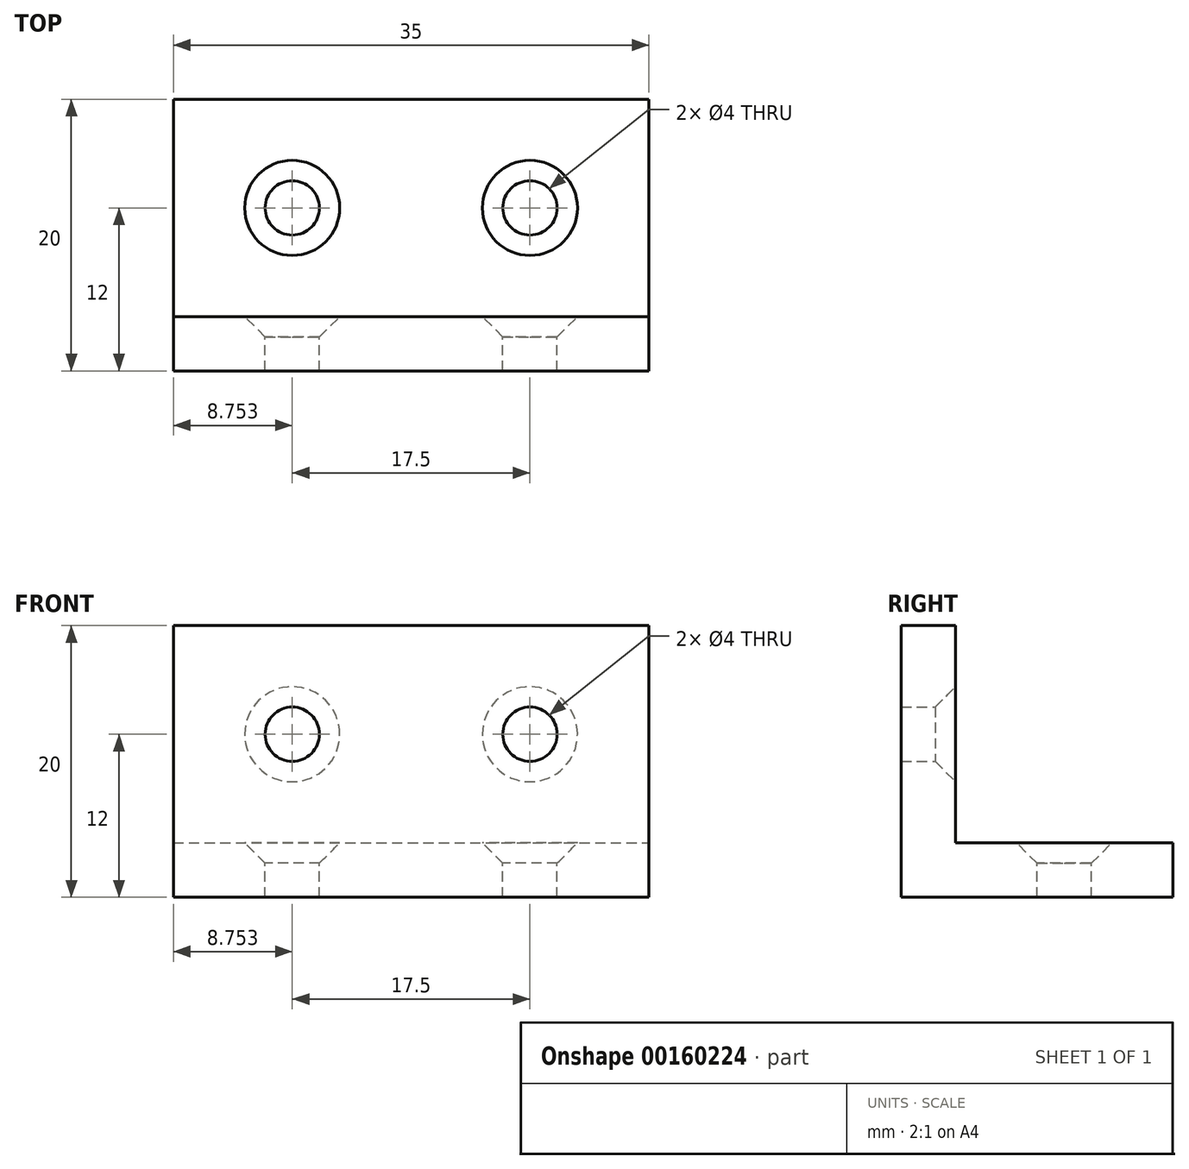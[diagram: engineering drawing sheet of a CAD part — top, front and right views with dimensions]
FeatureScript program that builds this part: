
annotation { "Feature Type Name" : "Feature", "Feature Type Description" : "" }
export const myFeature = defineFeature(function(context is Context, id is Id, definition is map)
    precondition{}
    {
        {
            var Q0;
            Q0=qCreatedBy(makeId("Top.planeOp"),FACE);
            var sketch = newSketch(context, id + "F0", { "sketchPlane" : qUnion([Q0])});
            skLineSegment(sketch, "E0.bottom", {"start": v(-15.22, 0) * mm, "end": v(19.78, 0) * mm});
            skLineSegment(sketch, "E0.top", {"start": v(-15.22, 20) * mm, "end": v(19.78, 20) * mm});
            skLineSegment(sketch, "E0.left", {"start": v(-15.22, 0) * mm, "end": v(-15.22, 20) * mm});
            skLineSegment(sketch, "E0.right", {"start": v(19.78, 0) * mm, "end": v(19.78, 20) * mm});
            skSolve(sketch);
        }
        {
            var Q0;
            Q0=makeQuery(id+"F0.imprint","IMPRINT",FACE,{"disambiguationData":[TD([[makeQuery(id+"F0.imprint","IMPRINT",EDGE,{"derivedFrom":sQuery(id+"F0.wireOp",EDGE,"E0.bottom")}),1.0]])]});
            extrude(context, id + "F1", {"entities" : qUnion([Q0]), "depth" : 4 * mm});
        }
        {
            var Q0;
            Q0=makeQuery(id+"F1.opExtrude","CAP_FACE",FACE,{"disambiguationData":[OSD([sQuery(id+"F0.wireOp",EDGE,"E0.bottom"),sQuery(id+"F0.wireOp",EDGE,"E0.top"),sQuery(id+"F0.wireOp",EDGE,"E0.left"),sQuery(id+"F0.wireOp",EDGE,"E0.right")])],"isStart":false});
            var sketch = newSketch(context, id + "F2", { "sketchPlane" : qUnion([Q0])});
            skLineSegment(sketch, "E1.bottom", {"start": v(-15.22, 0) * mm, "end": v(19.78, 0) * mm});
            skLineSegment(sketch, "E1.top", {"start": v(-15.22, 4) * mm, "end": v(19.78, 4) * mm});
            skLineSegment(sketch, "E1.left", {"start": v(-15.22, 0) * mm, "end": v(-15.22, 4) * mm});
            skLineSegment(sketch, "E1.right", {"start": v(19.78, 0) * mm, "end": v(19.78, 4) * mm});
            skSolve(sketch);
        }
        {
            var Q0;
            Q0=makeQuery(id+"F2.imprint","IMPRINT",FACE,{"disambiguationData":[TD([[makeQuery(id+"F2.imprint","IMPRINT",EDGE,{"derivedFrom":sQuery(id+"F2.wireOp",EDGE,"E1.bottom")}),1.0]])]});
            extrude(context, id + "F3", {"entities" : qUnion([Q0]), "operationType" : NewBodyOperationType.ADD, "depth" : 16 * mm});
        }
        {
            var Q0;
            Q0=makeQuery(id+"F3.opExtrude","SWEPT_FACE",FACE,{"disambiguationData":[OSD([sQuery(id+"F2.wireOp",EDGE,"E1.top")])]});
            var sketch = newSketch(context, id + "F4", { "sketchPlane" : qUnion([Q0])});
            skPoint(sketch, "E2", {"position": v(-11.03, 12) * mm});
            skPoint(sketch, "E3", {"position": v(6.47, 12) * mm});
            skSolve(sketch);
        }
        {
            var Q0;
            Q0=makeQuery(id+"F1.opExtrude","CAP_FACE",FACE,{"disambiguationData":[OSD([sQuery(id+"F0.wireOp",EDGE,"E0.bottom"),sQuery(id+"F0.wireOp",EDGE,"E0.top"),sQuery(id+"F0.wireOp",EDGE,"E0.left"),sQuery(id+"F0.wireOp",EDGE,"E0.right")])],"isStart":false});
            var sketch = newSketch(context, id + "F5", { "sketchPlane" : qUnion([Q0])});
            skPoint(sketch, "E4", {"position": v(-6.47, 12) * mm});
            skPoint(sketch, "E5", {"position": v(11.03, 12) * mm});
            skSolve(sketch);
        }
        {
            var Q0;
            Q0=sQuery(id+"F5.wireOp",VERTEX,"E5");
            var Q1;
            Q1=sQuery(id+"F5.wireOp",VERTEX,"E4");
            var Q2;
            Q2=sQuery(id+"F4.wireOp",VERTEX,"E3");
            var Q3;
            Q3=sQuery(id+"F4.wireOp",VERTEX,"E2");
            var Q4;
            Q4=makeQuery(id+"F1.opExtrude","SWEPT_BODY",BODY,{"disambiguationData":[OSD([sQuery(id+"F0.wireOp",EDGE,"E0.bottom"),sQuery(id+"F0.wireOp",EDGE,"E0.top"),sQuery(id+"F0.wireOp",EDGE,"E0.left"),sQuery(id+"F0.wireOp",EDGE,"E0.right")])]});
            hole(context, id + "F6", {"style" : HoleStyle.C_SINK, "endStyle" : HoleEndStyle.THROUGH, "holeDiameter" : 4 * mm, "cSinkDiameter" : 7 * mm, "cSinkAngle" : 90 * degree, "startFromSketch" : true, "locations" : qUnion([Q0, Q1, Q2, Q3]), "scope" : qUnion([Q4]), "isTappedThrough" : true});
        }
    });
